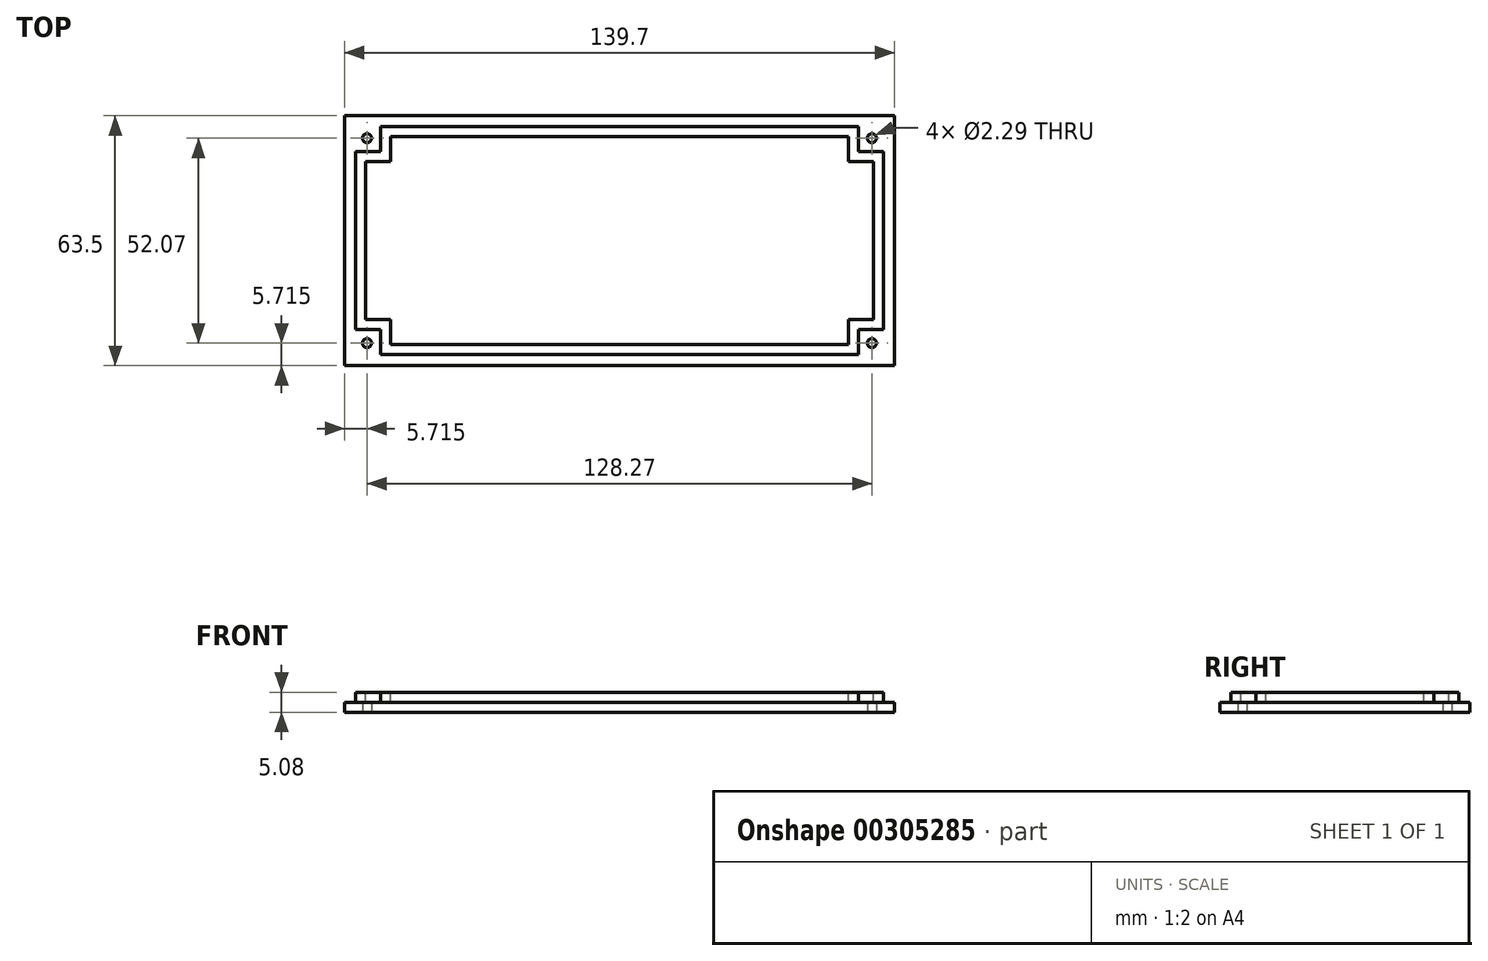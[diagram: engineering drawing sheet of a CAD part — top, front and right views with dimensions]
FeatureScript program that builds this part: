
annotation { "Feature Type Name" : "Feature", "Feature Type Description" : "" }
export const myFeature = defineFeature(function(context is Context, id is Id, definition is map)
    precondition{}
    {
        {
            var Q0;
            Q0=qCreatedBy(makeId("Top.planeOp"),FACE);
            var sketch = newSketch(context, id + "F0", { "sketchPlane" : qUnion([Q0])});
            skLineSegment(sketch, "E0.bottom", {"start": v(69.85, -31.75) * mm, "end": v(-69.85, -31.75) * mm});
            skLineSegment(sketch, "E0.top", {"start": v(69.85, 31.75) * mm, "end": v(-69.85, 31.75) * mm});
            skLineSegment(sketch, "E0.left", {"start": v(69.85, -31.75) * mm, "end": v(69.85, 31.75) * mm});
            skLineSegment(sketch, "E0.right", {"start": v(-69.85, -31.75) * mm, "end": v(-69.85, 31.75) * mm});
            skPoint(sketch, "E0.middle", {"position": v(0, 0) * mm});
            skSolve(sketch);
        }
        {
            var Q0;
            Q0=makeQuery(id+"F0.imprint","IMPRINT",FACE,{"disambiguationData":[TD([[makeQuery(id+"F0.imprint","IMPRINT",EDGE,{"derivedFrom":sQuery(id+"F0.wireOp",EDGE,"E0.bottom")}),-1.0]])]});
            extrude(context, id + "F1", {"entities" : qUnion([Q0]), "depth" : 2.54 * mm});
        }
        {
            var Q0;
            Q0=makeQuery(id+"F1.opExtrude","CAP_FACE",FACE,{"disambiguationData":[OSD([sQuery(id+"F0.wireOp",EDGE,"E0.bottom"),sQuery(id+"F0.wireOp",EDGE,"E0.top"),sQuery(id+"F0.wireOp",EDGE,"E0.left"),sQuery(id+"F0.wireOp",EDGE,"E0.right")])],"isStart":false});
            var sketch = newSketch(context, id + "F2", { "sketchPlane" : qUnion([Q0])});
            skLineSegment(sketch, "E1.0", {"start": v(67.06, -28.96) * mm, "end": v(67.06, 28.96) * mm});
            skLineSegment(sketch, "E1.1", {"start": v(-67.06, -28.96) * mm, "end": v(67.06, -28.96) * mm});
            skLineSegment(sketch, "E1.2", {"start": v(-67.06, 28.96) * mm, "end": v(-67.06, -28.96) * mm});
            skLineSegment(sketch, "E1.3", {"start": v(67.06, 28.96) * mm, "end": v(-67.06, 28.96) * mm});
            skLineSegment(sketch, "E2.0", {"start": v(76.2, -38.1) * mm, "end": v(76.2, 38.1) * mm});
            skLineSegment(sketch, "E2.1", {"start": v(-76.2, -38.1) * mm, "end": v(76.2, -38.1) * mm});
            skLineSegment(sketch, "E2.2", {"start": v(-76.2, 38.1) * mm, "end": v(-76.2, -38.1) * mm});
            skLineSegment(sketch, "E2.3", {"start": v(76.2, 38.1) * mm, "end": v(-76.2, 38.1) * mm});
            skSolve(sketch);
        }
        {
            var Q0;
            Q0=makeQuery(id+"F2.imprint","IMPRINT",FACE,{"disambiguationData":[TD([[makeQuery(id+"F2.imprint","IMPRINT",EDGE,{"derivedFrom":sQuery(id+"F2.wireOp",EDGE,"E1.0")}),1.0]])]});
            extrude(context, id + "F3", {"entities" : qUnion([Q0]), "operationType" : NewBodyOperationType.ADD, "depth" : 2.54 * mm});
        }
        {
            var Q0;
            Q0=makeQuery(id+"F3.opExtrude","CAP_FACE",FACE,{"disambiguationData":[OSD([sQuery(id+"F2.wireOp",EDGE,"E1.0"),sQuery(id+"F2.wireOp",EDGE,"E1.1"),sQuery(id+"F2.wireOp",EDGE,"E1.2"),sQuery(id+"F2.wireOp",EDGE,"E1.3")])],"isStart":false});
            var sketch = newSketch(context, id + "F4", { "sketchPlane" : qUnion([Q0])});
            skLineSegment(sketch, "E3.bottom", {"start": v(-67.06, 28.96) * mm, "end": v(-60.7, 28.96) * mm});
            skLineSegment(sketch, "E3.top", {"start": v(-67.06, 22.6) * mm, "end": v(-60.7, 22.6) * mm});
            skLineSegment(sketch, "E3.left", {"start": v(-67.06, 28.96) * mm, "end": v(-67.06, 22.6) * mm});
            skLineSegment(sketch, "E3.right", {"start": v(-60.7, 28.96) * mm, "end": v(-60.7, 22.6) * mm});
            skLineSegment(sketch, "E4", {"start": v(0, 28.96) * mm, "end": v(0, -28.96) * mm, "construction": true});
            skLineSegment(sketch, "E5", {"start": v(-67.06, 0) * mm, "end": v(67.06, 0) * mm, "construction": true});
            skLineSegment(sketch, "E6.MirrorCS", {"start": v(60.7, 28.96) * mm, "end": v(60.7, 22.6) * mm});
            skLineSegment(sketch, "E7.MirrorCS", {"start": v(67.06, 28.96) * mm, "end": v(67.06, 22.6) * mm});
            skLineSegment(sketch, "E8.MirrorCS", {"start": v(67.06, 22.6) * mm, "end": v(60.7, 22.6) * mm});
            skLineSegment(sketch, "E9.MirrorCS", {"start": v(67.06, 28.96) * mm, "end": v(60.7, 28.96) * mm});
            skLineSegment(sketch, "E10.MirrorCS", {"start": v(-60.7, -28.96) * mm, "end": v(-60.7, -22.6) * mm});
            skLineSegment(sketch, "E11.MirrorCS", {"start": v(-67.06, -28.96) * mm, "end": v(-60.7, -28.96) * mm});
            skLineSegment(sketch, "E12.MirrorCS", {"start": v(-67.06, -28.96) * mm, "end": v(-67.06, -22.6) * mm});
            skLineSegment(sketch, "E13.MirrorCS", {"start": v(-67.06, -22.6) * mm, "end": v(-60.7, -22.6) * mm});
            skLineSegment(sketch, "E14.MirrorCS", {"start": v(60.7, -28.96) * mm, "end": v(60.7, -22.6) * mm});
            skLineSegment(sketch, "E15.MirrorCS", {"start": v(67.06, -28.96) * mm, "end": v(67.06, -22.6) * mm});
            skLineSegment(sketch, "E16.MirrorCS", {"start": v(67.06, -22.6) * mm, "end": v(60.7, -22.6) * mm});
            skLineSegment(sketch, "E17.MirrorCS", {"start": v(67.06, -28.96) * mm, "end": v(60.7, -28.96) * mm});
            skSolve(sketch);
        }
        {
            var Q0;
            Q0 = qSketchRegion(id + "F4", true);
            extrude(context, id + "F5", {"entities" : qUnion([Q0]), "operationType" : NewBodyOperationType.REMOVE, "oppositeDirection" : true, "depth" : 2.54 * mm});
        }
        {
            var Q0;
            Q0=makeQuery(id+"F3.opExtrude","CAP_FACE",FACE,{"disambiguationData":[OSD([sQuery(id+"F2.wireOp",EDGE,"E1.0"),sQuery(id+"F2.wireOp",EDGE,"E1.1"),sQuery(id+"F2.wireOp",EDGE,"E1.2"),sQuery(id+"F2.wireOp",EDGE,"E1.3")])],"isStart":false});
            var sketch = newSketch(context, id + "F6", { "sketchPlane" : qUnion([Q0])});
            skLineSegment(sketch, "E18.0", {"start": v(58.17, 20.07) * mm, "end": v(58.17, 26.42) * mm});
            skLineSegment(sketch, "E18.1", {"start": v(-64.52, -20.07) * mm, "end": v(-58.17, -20.07) * mm});
            skLineSegment(sketch, "E18.2", {"start": v(-64.52, 20.07) * mm, "end": v(-64.52, -20.07) * mm});
            skLineSegment(sketch, "E18.3", {"start": v(-58.17, 20.07) * mm, "end": v(-64.52, 20.07) * mm});
            skLineSegment(sketch, "E18.4", {"start": v(-58.17, 26.42) * mm, "end": v(-58.17, 20.07) * mm});
            skLineSegment(sketch, "E18.5", {"start": v(-58.17, -20.07) * mm, "end": v(-58.17, -26.42) * mm});
            skLineSegment(sketch, "E18.6", {"start": v(58.17, 26.42) * mm, "end": v(-58.17, 26.42) * mm});
            skLineSegment(sketch, "E18.7", {"start": v(-58.17, -26.42) * mm, "end": v(58.17, -26.42) * mm});
            skLineSegment(sketch, "E18.8", {"start": v(58.17, -26.42) * mm, "end": v(58.17, -20.07) * mm});
            skLineSegment(sketch, "E18.9", {"start": v(58.17, -20.07) * mm, "end": v(64.52, -20.07) * mm});
            skLineSegment(sketch, "E18.10", {"start": v(64.52, -20.07) * mm, "end": v(64.52, 20.07) * mm});
            skLineSegment(sketch, "E18.11", {"start": v(64.52, 20.07) * mm, "end": v(58.17, 20.07) * mm});
            skLineSegment(sketch, "E19.0", {"start": v(67.06, 28.96) * mm, "end": v(67.06, 35.3) * mm});
            skLineSegment(sketch, "E19.1", {"start": v(-73.4, -28.96) * mm, "end": v(-67.06, -28.96) * mm});
            skLineSegment(sketch, "E19.2", {"start": v(-73.4, 28.96) * mm, "end": v(-73.4, -28.96) * mm});
            skLineSegment(sketch, "E19.3", {"start": v(-67.06, 28.96) * mm, "end": v(-73.4, 28.96) * mm});
            skLineSegment(sketch, "E19.4", {"start": v(-67.06, 35.3) * mm, "end": v(-67.06, 28.96) * mm});
            skLineSegment(sketch, "E19.5", {"start": v(-67.06, -28.96) * mm, "end": v(-67.06, -35.3) * mm});
            skLineSegment(sketch, "E19.6", {"start": v(67.06, 35.3) * mm, "end": v(-67.06, 35.3) * mm});
            skLineSegment(sketch, "E19.7", {"start": v(-67.06, -35.3) * mm, "end": v(67.06, -35.3) * mm});
            skLineSegment(sketch, "E19.8", {"start": v(67.06, -35.3) * mm, "end": v(67.06, -28.96) * mm});
            skLineSegment(sketch, "E19.9", {"start": v(67.06, -28.96) * mm, "end": v(73.4, -28.96) * mm});
            skLineSegment(sketch, "E19.10", {"start": v(73.4, -28.96) * mm, "end": v(73.4, 28.96) * mm});
            skLineSegment(sketch, "E19.11", {"start": v(73.4, 28.96) * mm, "end": v(67.06, 28.96) * mm});
            skSolve(sketch);
        }
        {
            var Q0;
            Q0=makeQuery(id+"F6.imprint","IMPRINT",FACE,{"disambiguationData":[TD([[makeQuery(id+"F6.imprint","IMPRINT",EDGE,{"derivedFrom":sQuery(id+"F6.wireOp",EDGE,"E18.0")}),1.0]])]});
            extrude(context, id + "F7", {"entities" : qUnion([Q0]), "operationType" : NewBodyOperationType.REMOVE, "oppositeDirection" : true, "depth" : 2.54 * mm});
        }
        {
            var Q0;
            Q0=makeQuery(id+"F1.opExtrude","CAP_FACE",FACE,{"disambiguationData":[OSD([sQuery(id+"F0.wireOp",EDGE,"E0.bottom"),sQuery(id+"F0.wireOp",EDGE,"E0.top"),sQuery(id+"F0.wireOp",EDGE,"E0.left"),sQuery(id+"F0.wireOp",EDGE,"E0.right")])],"isStart":true});
            var sketch = newSketch(context, id + "F8", { "sketchPlane" : qUnion([Q0])});
            skCircle(sketch, "E20", {"center": v(64.14, 26.04) * mm, "radius": 1.14 * mm});
            skLineSegment(sketch, "E21", {"start": v(0, 31.75) * mm, "end": v(0, -31.75) * mm, "construction": true});
            skLineSegment(sketch, "E22", {"start": v(-69.85, 0) * mm, "end": v(69.85, 0) * mm, "construction": true});
            skCircle(sketch, "E23.MirrorC", {"center": v(-64.14, 26.03) * mm, "radius": 1.14 * mm});
            skCircle(sketch, "E24.MirrorC", {"center": v(64.14, -26.04) * mm, "radius": 1.14 * mm});
            skCircle(sketch, "E25.MirrorC", {"center": v(-64.14, -26.03) * mm, "radius": 1.14 * mm});
            skSolve(sketch);
        }
        {
            var Q0;
            Q0 = qSketchRegion(id + "F8", true);
            extrude(context, id + "F9", {"entities" : qUnion([Q0]), "operationType" : NewBodyOperationType.REMOVE, "endBound" : BoundingType.UP_TO_NEXT, "oppositeDirection" : true, "depth" : 25.4 * mm});
        }
    });
